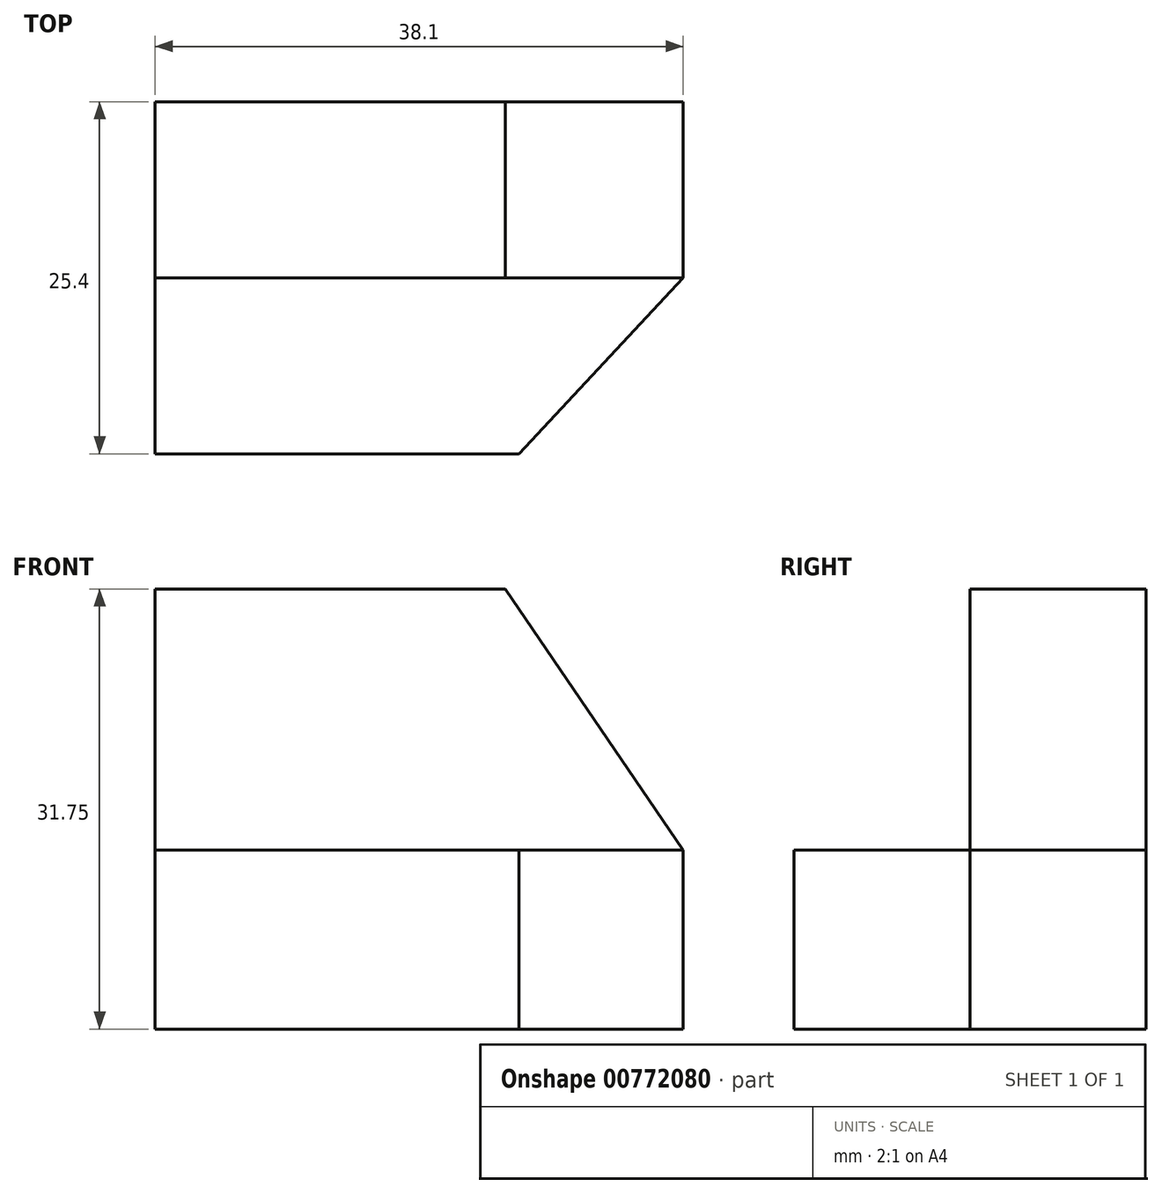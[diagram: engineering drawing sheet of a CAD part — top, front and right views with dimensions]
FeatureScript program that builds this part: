
annotation { "Feature Type Name" : "Feature", "Feature Type Description" : "" }
export const myFeature = defineFeature(function(context is Context, id is Id, definition is map)
    precondition{}
    {
        {
            var Q0;
            Q0=qCreatedBy(makeId("Front.planeOp"),FACE);
            var sketch = newSketch(context, id + "F0", { "sketchPlane" : qUnion([Q0])});
            skLineSegment(sketch, "E0", {"start": v(0, 1.35) * mm, "end": v(1.5, 0) * mm});
            skLineSegment(sketch, "E1", {"start": v(0, 0) * mm, "end": v(38.1, 0) * mm});
            skLineSegment(sketch, "E2", {"start": v(38.1, 0) * mm, "end": v(38.1, 31.75) * mm});
            skLineSegment(sketch, "E3", {"start": v(38.1, 31.75) * mm, "end": v(0, 31.75) * mm});
            skLineSegment(sketch, "E4", {"start": v(0, 31.75) * mm, "end": v(0, 0) * mm});
            skSolve(sketch);
        }
        {
            var Q0;
            Q0 = qSketchRegion(id + "F0", true);
            extrude(context, id + "F1", {"entities" : qUnion([Q0]), "depth" : 25.4 * mm, "offsetDistance" : 25.4 * mm});
        }
        {
            var Q0;
            Q0=makeQuery(id+"F1.opExtrude","CAP_FACE",FACE,{"disambiguationData":[OSD([sQuery(id+"F0.wireOp",EDGE,"E1"),sQuery(id+"F0.wireOp",EDGE,"E2"),sQuery(id+"F0.wireOp",EDGE,"E3"),sQuery(id+"F0.wireOp",EDGE,"E4")])],"isStart":false});
            var sketch = newSketch(context, id + "F2", { "sketchPlane" : qUnion([Q0])});
            skLineSegment(sketch, "E5", {"start": v(0, 31.75) * mm, "end": v(25.27, 31.75) * mm});
            skLineSegment(sketch, "E6", {"start": v(38.1, 0) * mm, "end": v(38.1, 12.9) * mm});
            skLineSegment(sketch, "E7", {"start": v(25.27, 31.75) * mm, "end": v(38.1, 12.9) * mm});
            skSolve(sketch);
        }
        {
            var Q0;
            {var subQ0=sQuery(id+"F2.wireOp",EDGE,"E7");Q0=makeQuery(id+"F2.imprint","IMPRINT",FACE,{"disambiguationData":[TD([[makeQuery(id+"F2.imprint","IMPRINT",EDGE,{"derivedFrom":subQ0}),1.0]])]});}
            extrude(context, id + "F3", {"entities" : qUnion([Q0]), "operationType" : NewBodyOperationType.REMOVE, "endBound" : BoundingType.THROUGH_ALL, "oppositeDirection" : true, "depth" : 25.4 * mm, "offsetDistance" : 25.4 * mm});
        }
        {
            var Q0;
            Q0=makeQuery(id+"F1.opExtrude","CAP_FACE",FACE,{"disambiguationData":[OSD([sQuery(id+"F0.wireOp",EDGE,"E1"),sQuery(id+"F0.wireOp",EDGE,"E2"),sQuery(id+"F0.wireOp",EDGE,"E3"),sQuery(id+"F0.wireOp",EDGE,"E4")])],"isStart":false});
            var sketch = newSketch(context, id + "F4", { "sketchPlane" : qUnion([Q0])});
            skLineSegment(sketch, "E8", {"start": v(38.1, 12.9) * mm, "end": v(0, 12.9) * mm});
            skSolve(sketch);
        }
        {
            var Q0;
            {var subQ0=sQuery(id+"F4.wireOp",EDGE,"E8");Q0=makeQuery(id+"F4.imprint","IMPRINT",FACE,{"disambiguationData":[TD([[makeQuery(id+"F4.imprint","IMPRINT",EDGE,{"derivedFrom":subQ0}),-1.0]])]});}
            extrude(context, id + "F5", {"entities" : qUnion([Q0]), "operationType" : NewBodyOperationType.REMOVE, "oppositeDirection" : true, "depth" : 12.7 * mm, "offsetDistance" : 25.4 * mm});
        }
        {
            var Q0;
            Q0=makeQuery(id+"F5.boolean.opBoolean","COPY",FACE,{"derivedFrom":makeQuery(id+"F5.opExtrude","SWEPT_FACE",FACE,{"disambiguationData":[OSD([sQuery(id+"F4.wireOp",EDGE,"E8")])]})});
            var sketch = newSketch(context, id + "F6", { "sketchPlane" : qUnion([Q0])});
            skLineSegment(sketch, "E9", {"start": v(26.24, -25.4) * mm, "end": v(38.1, -12.7) * mm});
            skLineSegment(sketch, "E10", {"start": v(26.24, -25.4) * mm, "end": v(38.1, -25.4) * mm});
            skLineSegment(sketch, "E11", {"start": v(38.1, -25.4) * mm, "end": v(38.1, -12.7) * mm});
            skSolve(sketch);
        }
        {
            var Q0;
            Q0 = qSketchRegion(id + "F6", true);
            extrude(context, id + "F7", {"entities" : qUnion([Q0]), "operationType" : NewBodyOperationType.REMOVE, "endBound" : BoundingType.THROUGH_ALL, "oppositeDirection" : true, "depth" : 25.4 * mm, "offsetDistance" : 25.4 * mm});
        }
    });
